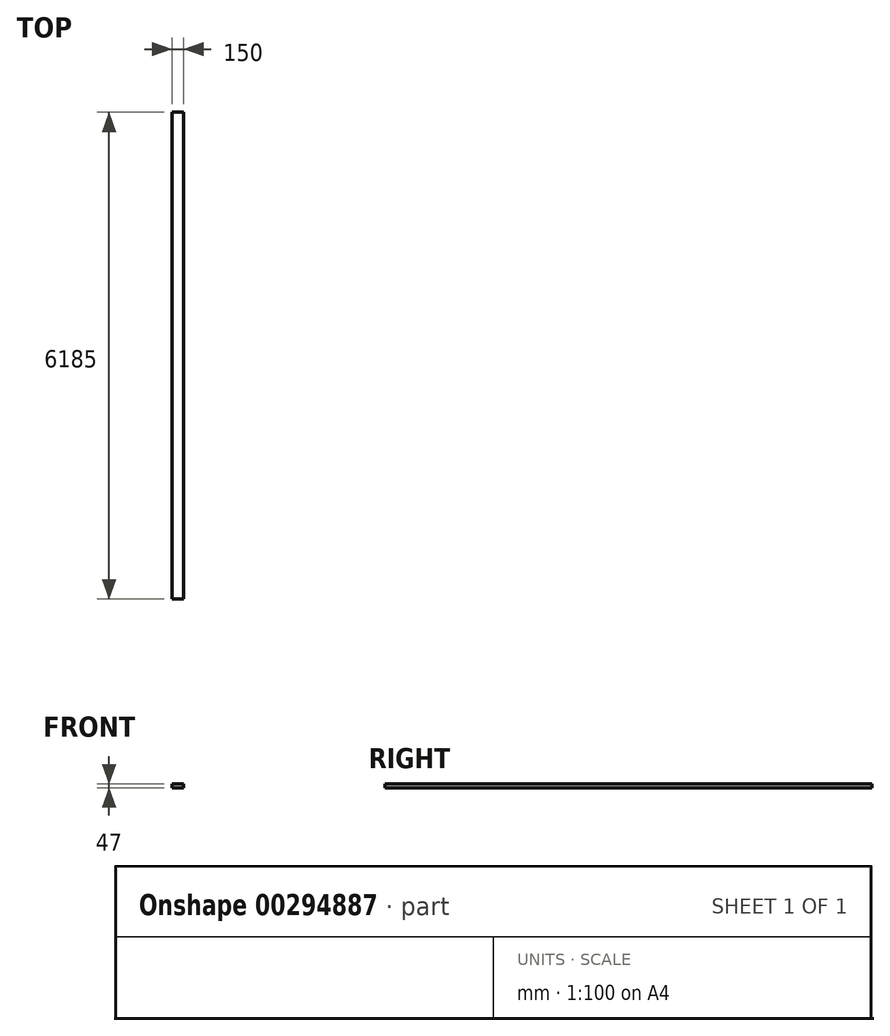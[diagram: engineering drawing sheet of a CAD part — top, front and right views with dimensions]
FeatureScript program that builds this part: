
annotation { "Feature Type Name" : "Feature", "Feature Type Description" : "" }
export const myFeature = defineFeature(function(context is Context, id is Id, definition is map)
    precondition{}
    {
        {
            var Q0;
            Q0=qCreatedBy(makeId("Front.planeOp"),FACE);
            var sketch = newSketch(context, id + "F0", { "sketchPlane" : qUnion([Q0])});
            skLineSegment(sketch, "E0.bottom", {"start": v(75, 23.5) * mm, "end": v(-75, 23.5) * mm});
            skLineSegment(sketch, "E0.top", {"start": v(75, -23.5) * mm, "end": v(-75, -23.5) * mm});
            skLineSegment(sketch, "E0.left", {"start": v(75, 23.5) * mm, "end": v(75, -23.5) * mm});
            skLineSegment(sketch, "E0.right", {"start": v(-75, 23.5) * mm, "end": v(-75, -23.5) * mm});
            skPoint(sketch, "E0.middle", {"position": v(0, 0) * mm});
            skSolve(sketch);
        }
        {
            var Q0;
            Q0 = qSketchRegion(id + "F0", true);
            extrude(context, id + "F1", {"entities" : qUnion([Q0]), "depth" : 6185 * mm});
        }
    });
